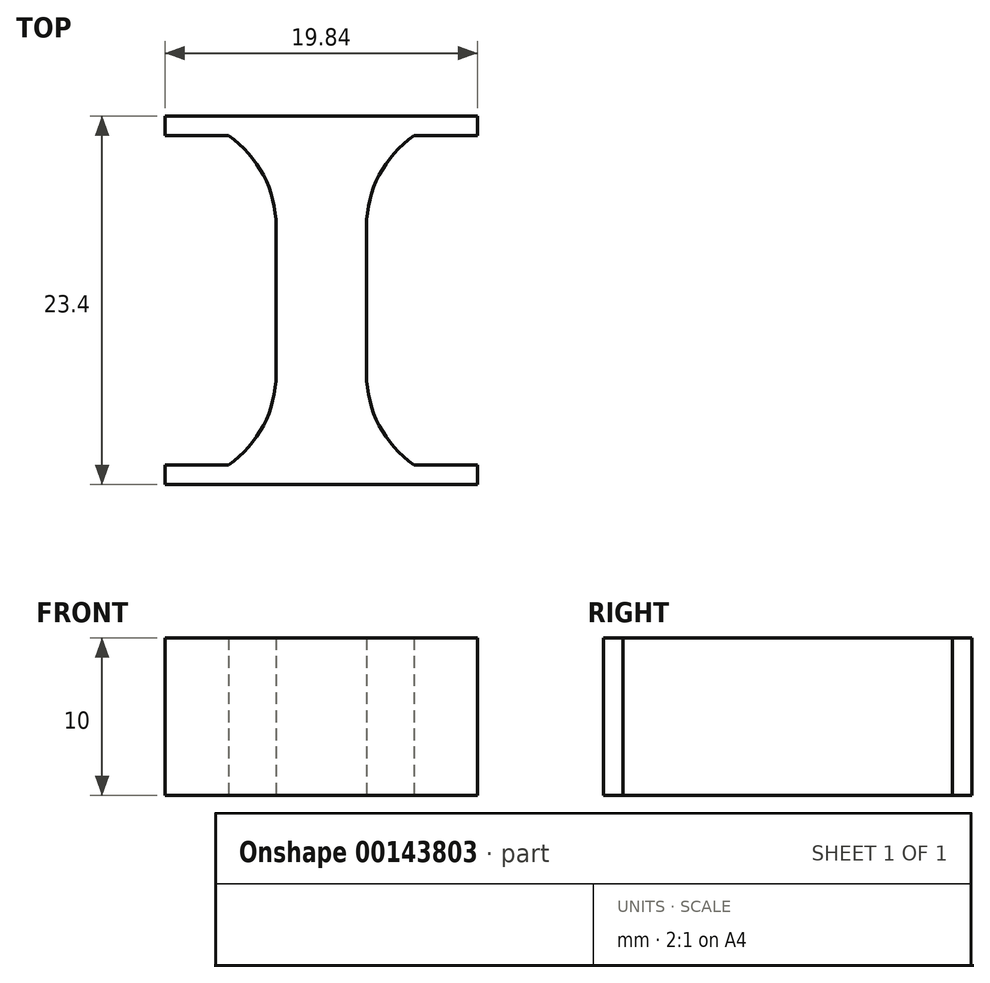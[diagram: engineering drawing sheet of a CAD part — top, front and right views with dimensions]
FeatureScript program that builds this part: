
annotation { "Feature Type Name" : "Feature", "Feature Type Description" : "" }
export const myFeature = defineFeature(function(context is Context, id is Id, definition is map)
    precondition{}
    {
        {
            var Q0;
            Q0=qCreatedBy(makeId("Top.planeOp"),FACE);
            var sketch = newSketch(context, id + "F0", { "sketchPlane" : qUnion([Q0])});
            skLineSegment(sketch, "E0", {"start": v(0, 0) * mm, "end": v(2.87, 0) * mm});
            skLineSegment(sketch, "E1", {"start": v(2.87, 0) * mm, "end": v(2.87, 4.7) * mm});
            skArc(sketch, "E2", {"start": v(9.92, 11.7) * mm, "mid": v(9.87, 11.7) * mm, "end": v(9.83, 11.7) * mm});
            skLineSegment(sketch, "E3", {"start": v(9.92, 11.7) * mm, "end": v(0, 11.7) * mm});
            skLineSegment(sketch, "E4.MirrorCS", {"start": v(0, 0) * mm, "end": v(-2.87, 0) * mm});
            skLineSegment(sketch, "E5.MirrorCS", {"start": v(-2.87, 0) * mm, "end": v(-2.87, 4.7) * mm});
            skArc(sketch, "E6.MirrorCS", {"start": v(-9.92, 11.7) * mm, "mid": v(-9.87, 11.7) * mm, "end": v(-9.83, 11.7) * mm});
            skLineSegment(sketch, "E7.MirrorCS", {"start": v(-9.92, 11.7) * mm, "end": v(0, 11.7) * mm});
            skLineSegment(sketch, "E8", {"start": v(9.92, 11.7) * mm, "end": v(9.92, 10.45) * mm});
            skLineSegment(sketch, "E9", {"start": v(9.92, 10.45) * mm, "end": v(5.88, 10.45) * mm});
            skLineSegment(sketch, "E10", {"start": v(-9.92, 11.7) * mm, "end": v(-9.92, 10.45) * mm});
            skArc(sketch, "E11.trimOffspring", {"start": v(-5.88, 10.45) * mm, "mid": v(-3.67, 7.94) * mm, "end": v(-2.88, 4.7) * mm});
            skLineSegment(sketch, "E12.trimOffspring", {"start": v(-5.88, 10.45) * mm, "end": v(-9.92, 10.45) * mm});
            skArc(sketch, "E13.trimOffspring", {"start": v(5.88, 10.45) * mm, "mid": v(3.67, 7.94) * mm, "end": v(2.88, 4.7) * mm});
            skArc(sketch, "E14.MirrorCS", {"start": v(9.92, -11.7) * mm, "mid": v(9.87, -11.7) * mm, "end": v(9.83, -11.7) * mm});
            skArc(sketch, "E15.MirrorCS", {"start": v(-9.92, -11.7) * mm, "mid": v(-9.87, -11.7) * mm, "end": v(-9.83, -11.7) * mm});
            skArc(sketch, "E16.MirrorCS", {"start": v(5.88, -10.45) * mm, "mid": v(3.67, -7.94) * mm, "end": v(2.88, -4.7) * mm});
            skLineSegment(sketch, "E17.MirrorCS", {"start": v(2.87, 0) * mm, "end": v(2.87, -4.7) * mm});
            skArc(sketch, "E18.MirrorCS", {"start": v(-5.88, -10.45) * mm, "mid": v(-3.67, -7.94) * mm, "end": v(-2.88, -4.7) * mm});
            skLineSegment(sketch, "E19.MirrorCS", {"start": v(9.92, -11.7) * mm, "end": v(0, -11.7) * mm});
            skLineSegment(sketch, "E20.MirrorCS", {"start": v(-2.87, 0) * mm, "end": v(-2.87, -4.7) * mm});
            skLineSegment(sketch, "E21.MirrorCS", {"start": v(-9.92, -11.7) * mm, "end": v(0, -11.7) * mm});
            skLineSegment(sketch, "E22.MirrorCS", {"start": v(9.92, -11.7) * mm, "end": v(9.92, -10.45) * mm});
            skLineSegment(sketch, "E23.MirrorCS", {"start": v(-9.92, -11.7) * mm, "end": v(-9.92, -10.45) * mm});
            skLineSegment(sketch, "E24.MirrorCS", {"start": v(-5.88, -10.45) * mm, "end": v(-9.92, -10.45) * mm});
            skLineSegment(sketch, "E25.MirrorCS", {"start": v(9.92, -10.45) * mm, "end": v(5.88, -10.45) * mm});
            skSolve(sketch);
        }
        {
            var Q0;
            {var subQ1=sQuery(id+"F0.wireOp",EDGE,"E22.MirrorCS");Q0=makeQuery(id+"F0.imprint","IMPRINT",FACE,{"disambiguationData":[TD([[makeQuery(id+"F0.imprint","IMPRINT",EDGE,{"derivedFrom":subQ1}),1.0]])]});}
            var Q1;
            Q1=makeQuery(id+"F0.imprint","IMPRINT",FACE,{"disambiguationData":[TD([[makeQuery(id+"F0.imprint","IMPRINT",EDGE,{"derivedFrom":sQuery(id+"F0.wireOp",EDGE,"E1")}),1.0]])]});
            extrude(context, id + "F1", {"entities" : qUnion([Q0, Q1]), "depth" : 10 * mm});
        }
    });
